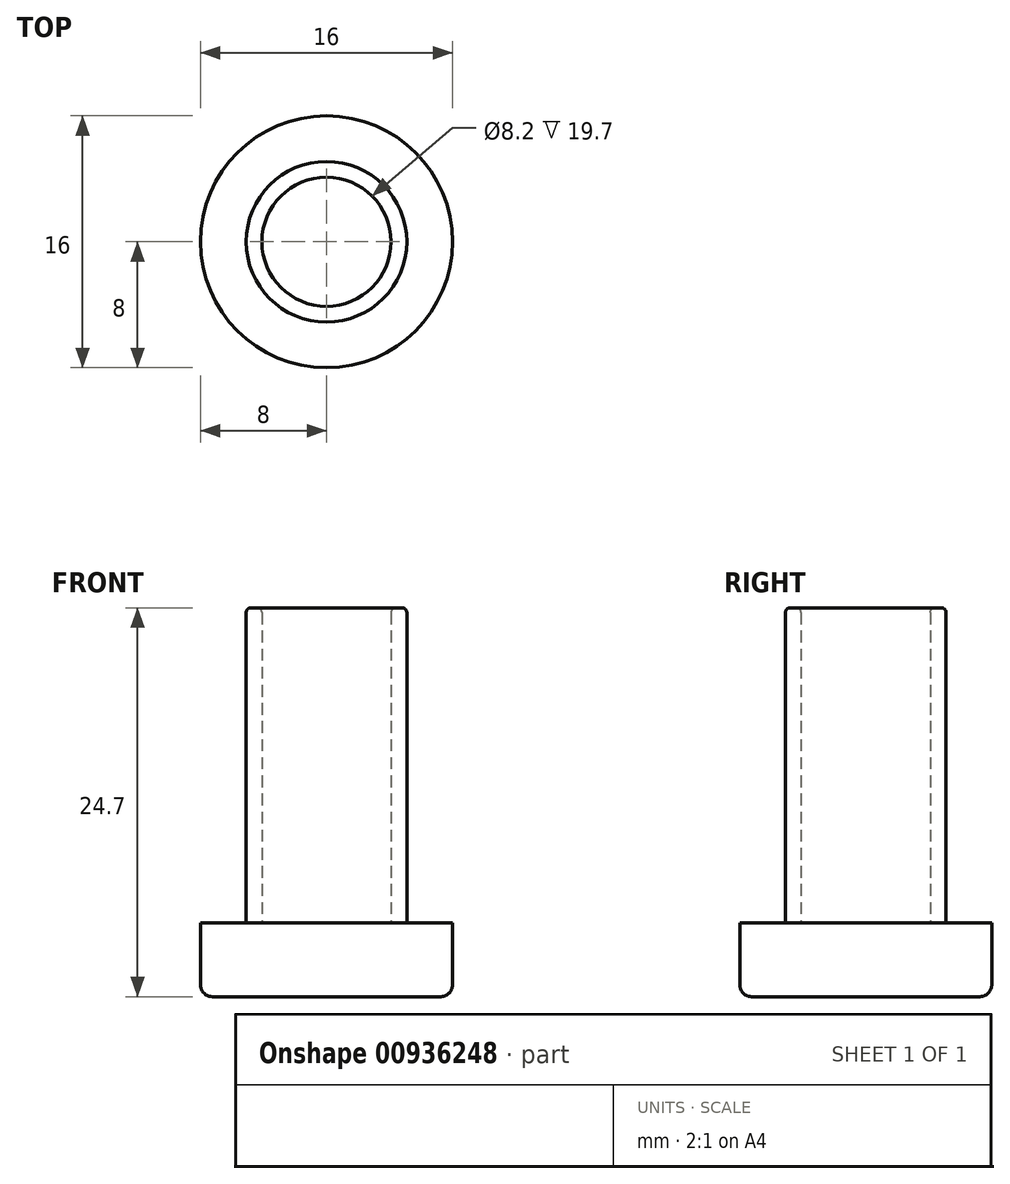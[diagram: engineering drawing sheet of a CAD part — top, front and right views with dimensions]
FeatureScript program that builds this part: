
annotation { "Feature Type Name" : "Feature", "Feature Type Description" : "" }
export const myFeature = defineFeature(function(context is Context, id is Id, definition is map)
    precondition{}
    {
        {
            var Q0;
            Q0=qCreatedBy(makeId("Top.planeOp"),FACE);
            var sketch = newSketch(context, id + "F0", { "sketchPlane" : qUnion([Q0])});
            skCircle(sketch, "E0", {"center": v(0, 0) * mm, "radius": 8 * mm});
            skCircle(sketch, "E1", {"center": v(0, 0) * mm, "radius": 5.1 * mm});
            skCircle(sketch, "E2", {"center": v(0, 0) * mm, "radius": 4.1 * mm});
            skSolve(sketch);
        }
        {
            var Q0;
            Q0=qSketchRegion(id+"F0",true);
            var Q1;
            Q1=makeQuery(id+"F0.imprint","IMPRINT",FACE,{"disambiguationData":[TD([[makeQuery(id+"F0.imprint","IMPRINT",EDGE,{"derivedFrom":sQuery(id+"F0.wireOp",EDGE,"E1")}),1.0]])]});
            var Q2;
            Q2=makeQuery(id+"F0.imprint","IMPRINT",FACE,{"disambiguationData":[TD([[makeQuery(id+"F0.imprint","IMPRINT",EDGE,{"derivedFrom":sQuery(id+"F0.wireOp",EDGE,"E2")}),1.0]])]});
            extrude(context, id + "F1", {"entities" : qUnion([Q0, Q1, Q2]), "depth" : 4.7 * mm, "offsetDistance" : 25.4 * mm});
        }
        {
            var Q0;
            Q0=makeQuery(id+"F0.imprint","IMPRINT",FACE,{"disambiguationData":[TD([[makeQuery(id+"F0.imprint","IMPRINT",EDGE,{"derivedFrom":sQuery(id+"F0.wireOp",EDGE,"E1")}),1.0]])]});
            extrude(context, id + "F2", {"entities" : qUnion([Q0]), "operationType" : NewBodyOperationType.ADD, "depth" : 24.7 * mm, "offsetDistance" : 25.4 * mm});
        }
        {
            var Q0;
            Q0=makeQuery(id+"F2.opExtrude","CAP_EDGE",EDGE,{"disambiguationData":[OSD([sQuery(id+"F0.wireOp",EDGE,"E1")])],"isStart":false});
            var Q1;
            Q1=makeQuery(id+"F2.opExtrude","CAP_EDGE",EDGE,{"disambiguationData":[OSD([sQuery(id+"F0.wireOp",EDGE,"E2")])],"isStart":false});
            fillet(context, id + "F3", {"entities" : qUnion([Q0, Q1]), "radius" : .3 * mm, "tangentPropagation" : true, "allowEdgeOverflow" : false});
        }
        {
            var Q0;
            Q0=makeQuery(id+"F1.opExtrude","CAP_EDGE",EDGE,{"disambiguationData":[OSD([sQuery(id+"F0.wireOp",EDGE,"E0")])],"isStart":true});
            fillet(context, id + "F4", {"entities" : qUnion([Q0]), "radius" : .75 * mm, "tangentPropagation" : true, "allowEdgeOverflow" : false});
        }
    });
